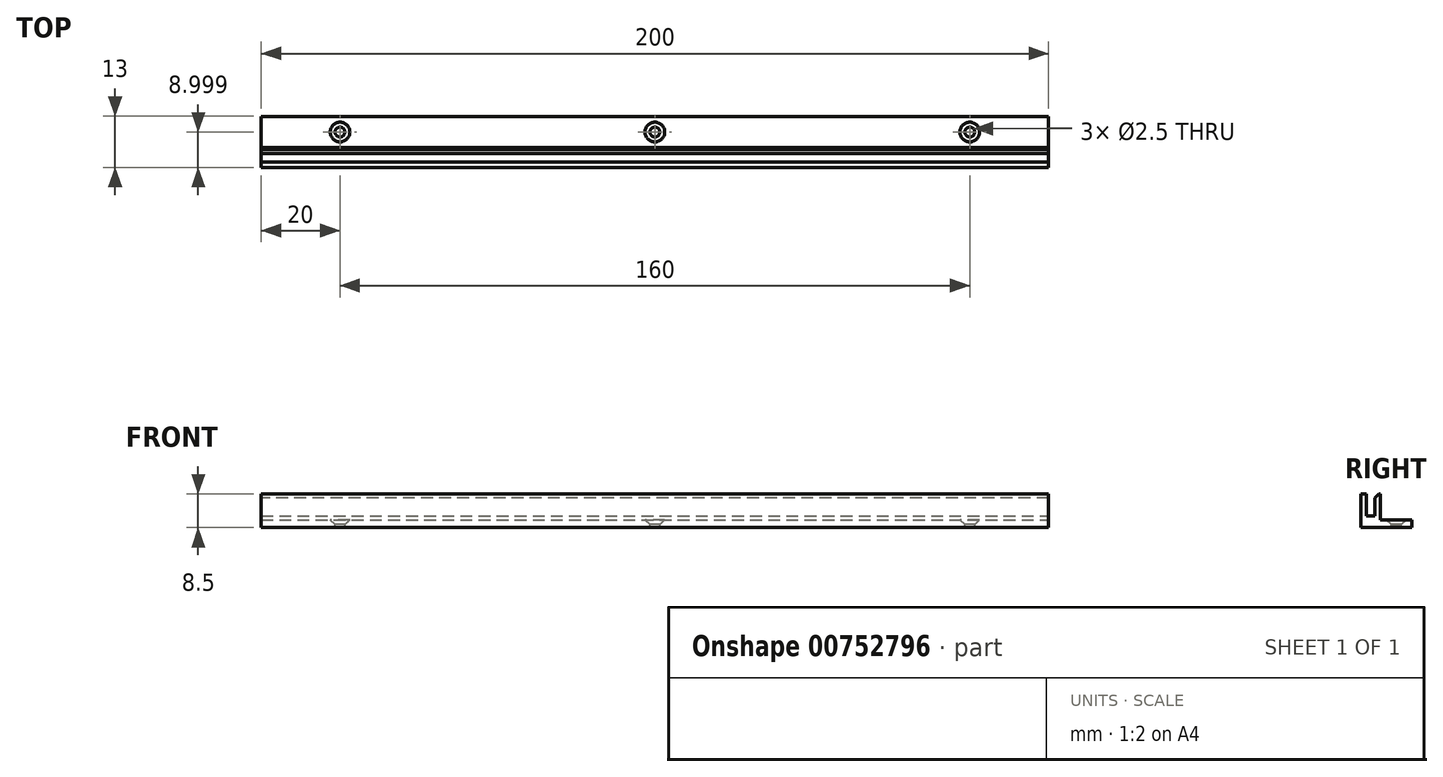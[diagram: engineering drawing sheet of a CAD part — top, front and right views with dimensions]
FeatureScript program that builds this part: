
annotation { "Feature Type Name" : "Feature", "Feature Type Description" : "" }
export const myFeature = defineFeature(function(context is Context, id is Id, definition is map)
    precondition{}
    {
        {
            var Q0;
            Q0=qCreatedBy(makeId("Top.planeOp"),FACE);
            var sketch = newSketch(context, id + "F0", { "sketchPlane" : qUnion([Q0])});
            skLineSegment(sketch, "E0.bottom", {"start": v(-100, 3.34) * mm, "end": v(100, 3.34) * mm});
            skLineSegment(sketch, "E0.top", {"start": v(-100, -1.66) * mm, "end": v(100, -1.66) * mm});
            skLineSegment(sketch, "E0.left", {"start": v(-100, 3.34) * mm, "end": v(-100, -1.66) * mm});
            skLineSegment(sketch, "E0.right", {"start": v(100, 3.34) * mm, "end": v(100, -1.66) * mm});
            skSolve(sketch);
        }
        {
            var Q0;
            Q0 = qSketchRegion(id + "F0", true);
            extrude(context, id + "F1", {"entities" : qUnion([Q0]), "depth" : 8.5 * mm, "offsetDistance" : 25 * mm});
        }
        {
            var Q0;
            Q0=makeQuery(id+"F1.opExtrude","CAP_FACE",FACE,{"disambiguationData":[OSD([sQuery(id+"F0.wireOp",EDGE,"E0.bottom"),sQuery(id+"F0.wireOp",EDGE,"E0.top"),sQuery(id+"F0.wireOp",EDGE,"E0.left"),sQuery(id+"F0.wireOp",EDGE,"E0.right")])],"isStart":false});
            var sketch = newSketch(context, id + "F2", { "sketchPlane" : qUnion([Q0])});
            skLineSegment(sketch, "E1.bottom", {"start": v(-100, 1.94) * mm, "end": v(100, 1.94) * mm});
            skLineSegment(sketch, "E1.top", {"start": v(-100, -0.26) * mm, "end": v(100, -0.26) * mm});
            skLineSegment(sketch, "E1.left", {"start": v(-100, 1.94) * mm, "end": v(-100, -0.26) * mm});
            skLineSegment(sketch, "E1.right", {"start": v(100, 1.94) * mm, "end": v(100, -0.26) * mm});
            skSolve(sketch);
        }
        {
            var Q0;
            Q0 = qSketchRegion(id + "F2", true);
            extrude(context, id + "F3", {"entities" : qUnion([Q0]), "operationType" : NewBodyOperationType.REMOVE, "oppositeDirection" : true, "depth" : 5.5 * mm, "offsetDistance" : 25 * mm});
        }
        {
            var Q0;
            Q0=makeQuery(id+"F1.opExtrude","SWEPT_FACE",FACE,{"disambiguationData":[OSD([sQuery(id+"F0.wireOp",EDGE,"E0.bottom")])]});
            var sketch = newSketch(context, id + "F4", { "sketchPlane" : qUnion([Q0])});
            skLineSegment(sketch, "E2.bottom", {"start": v(100, 2) * mm, "end": v(-100, 2) * mm});
            skLineSegment(sketch, "E2.top", {"start": v(100, 0) * mm, "end": v(-100, 0) * mm});
            skLineSegment(sketch, "E2.left", {"start": v(100, 2) * mm, "end": v(100, 0) * mm});
            skLineSegment(sketch, "E2.right", {"start": v(-100, 2) * mm, "end": v(-100, 0) * mm});
            skSolve(sketch);
        }
        {
            var Q0;
            Q0 = qSketchRegion(id + "F4", true);
            extrude(context, id + "F5", {"entities" : qUnion([Q0]), "operationType" : NewBodyOperationType.ADD, "depth" : 8 * mm, "offsetDistance" : 25 * mm});
        }
        {
            var Q0;
            Q0=makeQuery(id+"F5.opExtrude","SWEPT_FACE",FACE,{"disambiguationData":[OSD([sQuery(id+"F4.wireOp",EDGE,"E2.bottom")])]});
            var sketch = newSketch(context, id + "F6", { "sketchPlane" : qUnion([Q0])});
            skPoint(sketch, "E3", {"position": v(-80, 7.34) * mm});
            skPoint(sketch, "E4", {"position": v(0, 7.34) * mm});
            skPoint(sketch, "E5", {"position": v(80, 7.34) * mm});
            skSolve(sketch);
        }
        {
            var Q0;
            Q0=sQuery(id+"F6.wireOp",VERTEX,"E4");
            var Q1;
            Q1=sQuery(id+"F6.wireOp",VERTEX,"E5");
            var Q2;
            Q2=sQuery(id+"F6.wireOp",VERTEX,"E3");
            var Q3;
            Q3=makeQuery(id+"F1.opExtrude","SWEPT_BODY",BODY,{"disambiguationData":[OSD([sQuery(id+"F0.wireOp",EDGE,"E0.bottom"),sQuery(id+"F0.wireOp",EDGE,"E0.top"),sQuery(id+"F0.wireOp",EDGE,"E0.left"),sQuery(id+"F0.wireOp",EDGE,"E0.right")])]});
            hole(context, id + "F7", {"style" : HoleStyle.C_SINK, "endStyle" : HoleEndStyle.THROUGH, "holeDiameter" : 2.5 * mm, "cSinkDiameter" : 5 * mm, "cSinkAngle" : 90 * degree, "majorDiameter" : 5 * mm, "isTappedThrough" : true, "tappedDepth" : 12 * mm, "tapClearance" : 3, "locations" : qUnion([Q0, Q1, Q2]), "scope" : qUnion([Q3])});
        }
        {
            var Q0;
            Q0=makeQuery(id+"F3.boolean.opBoolean","COPY",EDGE,{"derivedFrom":makeQuery(id+"F3.opExtrude","CAP_EDGE",EDGE,{"disambiguationData":[OSD([sQuery(id+"F2.wireOp",EDGE,"E1.bottom")])],"isStart":true})});
            var Q1;
            Q1=makeQuery(id+"F3.boolean.opBoolean","COPY",EDGE,{"derivedFrom":makeQuery(id+"F3.opExtrude","CAP_EDGE",EDGE,{"disambiguationData":[OSD([sQuery(id+"F2.wireOp",EDGE,"E1.top")])],"isStart":true})});
            chamfer(context, id + "F8", {"entities" : qUnion([Q0, Q1]), "width" : 1 * mm, "tangentPropagation" : true});
        }
    });
